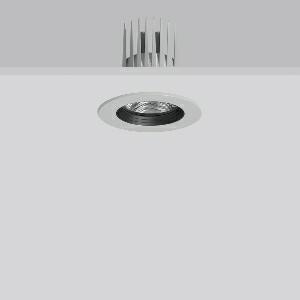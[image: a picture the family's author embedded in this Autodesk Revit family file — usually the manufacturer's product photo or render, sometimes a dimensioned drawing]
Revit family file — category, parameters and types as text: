
# Revit family: heledon_mini_e_901741_004_1_77ff
name_source: partatom
category: Lighting Fixtures
units: mm (PartAtom-declared; Revit-internal decimal feet)

## family parameters
Cut with Voids When Loaded = No
Host = Face
Light Source = No
Part Type = Normal
Room Calculation Point = No
Round Connector Dimension = Use Diameter
Shared = No

## types (1)
- HELEDON mini E (1 x LED Modul 940, 2600 lm, 4000)
    Apparent Load = 20 VA
    Approval mark = CE
    CIE Flux Codes = 99 100 100 100 100
    Color Rendering = 92
    Color Temperature = 4000
    Default Elevation = 1800 mm
    Description = Series: HELEDON mini
Round recessed downlight. Housing: die-cast aluminium, powder-coated. Black plastic ring and recessed LED to prevent glare from the side. Optical assembly with reflector made of MIRO-Silver with 98% total light reflection for outstanding efficiency - can be changed without tools. Best colour rendering index Ra>90. Suitable for Recessed ceiling mounting. Installation without tools thanks to spring fastening system. Including separate LED converter with connecting cable 600 mm.High quality converter without flickering and stroboscopic effect. Through-wiring box (5 pole) available as accessory. The following accessories can be mounted without use of tools: interchangeable lenses, decorative glasses, honeycomb louvre, clear and frosted diffusers, white interchangeable plastic ring. 
Colour: silver
Diameter: 124 mm
Height: 3 mm
Cut-out diameter: 114 mm
Recess height: 170 mm
Luminaire: recess height: 120 mm
Lamp: LED
Socket: without socket
Colour temperature: 4000K
Colour rendering index (CRI): 92
System power: 20 W
Rated luminous flux: 2600 lm
Luminous efficiency: 130 lm/W
Control gear: Regulated power supply
Protection class: II
Type of protection: IP 20
    Height = 0 mm  [stored 0 ft]
    Lamp = 1 x LED Modul 940
    Lamp Light Flux = 2600 lm
    Lamp count = 1
    Length = 124 mm  [stored 0.406824 ft]
    Lifetime = 50000 h
    Luminous efficacy = 130 lm/W
    Manufacturer = RZB
    ModVariant = No
    Model = 901741.004.1
    Mounting Place = Ceiling
    Mounting Type = Recessed
    Number of Poles = 1
    OnlyDefault = Yes
    Power Factor = 1
    Product Name = HELEDON mini E
    Product group = Recessed downlights
    ProductGroupID = 402
    Protection Class = Protection class II
    Protection Degree = IP 20
    RLX_Detail_Level = 1
    RLX_Emergency_Light_Flux = 0 lm
    RLX_Emergency_Type = 0
    RLX_Emergency_Type_DB = No
    RlxData = <blob elided: 126137 chars, md5=c91263bb>
    Socket = socket
    Standby Power = 0 W
    System Light Flux = 2600 lm
    System Power = 20 W
    Type Comments = Product without accessories
    Type Image = 901657.004.jpg
    URL = http://relux.com
    VarID = ---
    Voltage = 230 V
    Voltage Range = 220-240 V
    Weight = 0.00 kg
    Width = 0 mm  [stored 0 ft]

note: [stored X ft] marks values corroborated as IEEE doubles in the binary element streams (Revit-internal decimal feet)

## geometry (parser evidence)
native form markers: Blend x4, Sweep x10
no freeform markers — native parametric forms only
